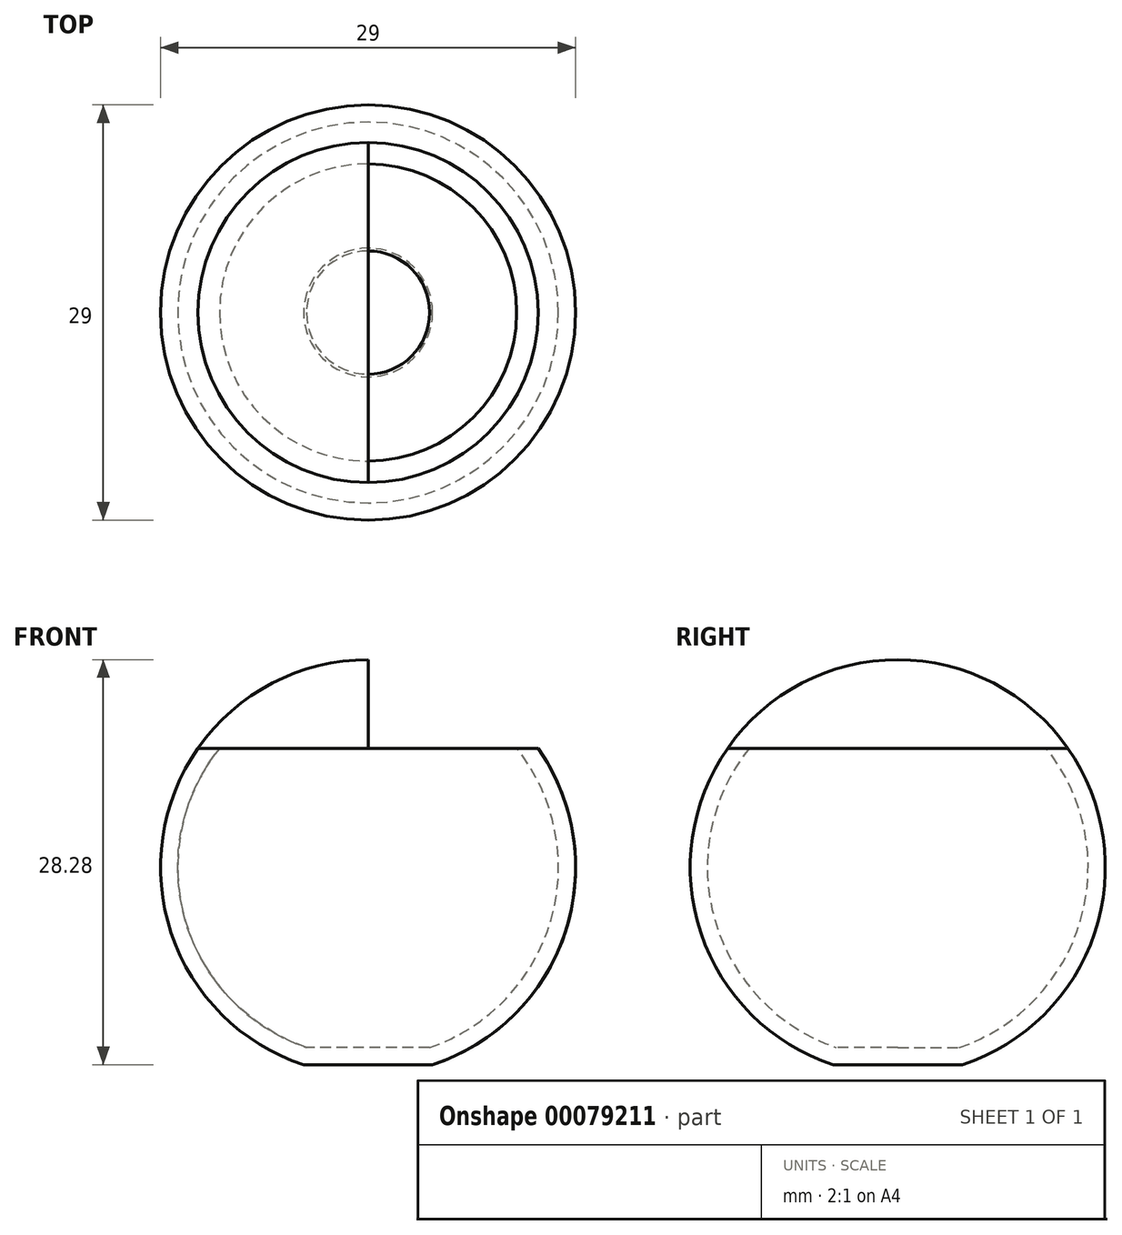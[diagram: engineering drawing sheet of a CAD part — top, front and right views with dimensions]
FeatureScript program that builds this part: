
annotation { "Feature Type Name" : "Feature", "Feature Type Description" : "" }
export const myFeature = defineFeature(function(context is Context, id is Id, definition is map)
    precondition{}
    {
        {
            var Q0;
            Q0=qCreatedBy(makeId("Front.planeOp"),FACE);
            var sketch = newSketch(context, id + "F0", { "sketchPlane" : qUnion([Q0])});
            skCircle(sketch, "E0", {"center": v(0, 0) * mm, "radius": 14.5 * mm, "construction": true});
            skLineSegment(sketch, "E1", {"start": v(-4.5, -13.78) * mm, "end": v(4.5, -13.78) * mm, "construction": true});
            skLineSegment(sketch, "E2", {"start": v(0, 14.5) * mm, "end": v(0, -13.78) * mm});
            skLineSegment(sketch, "E3", {"start": v(0, -13.78) * mm, "end": v(-4.5, -13.78) * mm});
            skLineSegment(sketch, "E4", {"start": v(-11.88, 8.32) * mm, "end": v(0, 25.28) * mm});
            skLineSegment(sketch, "E5", {"start": v(-11.88, 8.32) * mm, "end": v(0, 8.32) * mm});
            skArc(sketch, "E6", {"start": v(-11.88, 8.32) * mm, "mid": v(-13.75, -4.6) * mm, "end": v(-4.5, -13.78) * mm});
            skSolve(sketch);
        }
        {
            var Q0;
            Q0 = qSketchRegion(id + "F0", true);
            var Q1;
            Q1=sQuery(id+"F0.wireOp",EDGE,"E2");
            revolve(context, id + "F1", {"entities" : qUnion([Q0]), "axis" : qUnion([Q1]), "revolveType" : RevolveType.FULL});
        }
        {
            var Q0;
            Q0=makeQuery(id+"F1.opRevolve","SWEPT_FACE",FACE,{"disambiguationData":[OSD([sQuery(id+"F0.wireOp",EDGE,"E5")])]});
            shell(context, id + "F2", {"entities" : qUnion([Q0]), "thickness" : 1.2 * mm});
        }
        {
            var Q0;
            Q0=qCreatedBy(makeId("Front.planeOp"),FACE);
            var sketch = newSketch(context, id + "F3", { "sketchPlane" : qUnion([Q0])});
            skArc(sketch, "E7", {"start": v(0, 14.5) * mm, "mid": v(-6.7, 12.86) * mm, "end": v(-11.88, 8.32) * mm});
            skLineSegment(sketch, "E8", {"start": v(0, 14.5) * mm, "end": v(0, 8.31) * mm});
            skLineSegment(sketch, "E9", {"start": v(0, 8.31) * mm, "end": v(-11.88, 8.32) * mm});
            skSolve(sketch);
        }
        {
            var Q0;
            Q0=makeQuery(id+"F3.imprint","IMPRINT",FACE,{"disambiguationData":[TD([[makeQuery(id+"F3.imprint","IMPRINT",EDGE,{"derivedFrom":sQuery(id+"F3.wireOp",EDGE,"E7")}),1.0]])]});
            var Q1;
            Q1=sQuery(id+"F3.wireOp",EDGE,"E8");
            revolve(context, id + "F4", {"entities" : qUnion([Q0]), "axis" : qUnion([Q1]), "revolveType" : RevolveType.TWO_DIRECTIONS, "oppositeDirection" : true, "angle" : 90 * degree, "angleBack" : 270 * degree});
        }
    });
